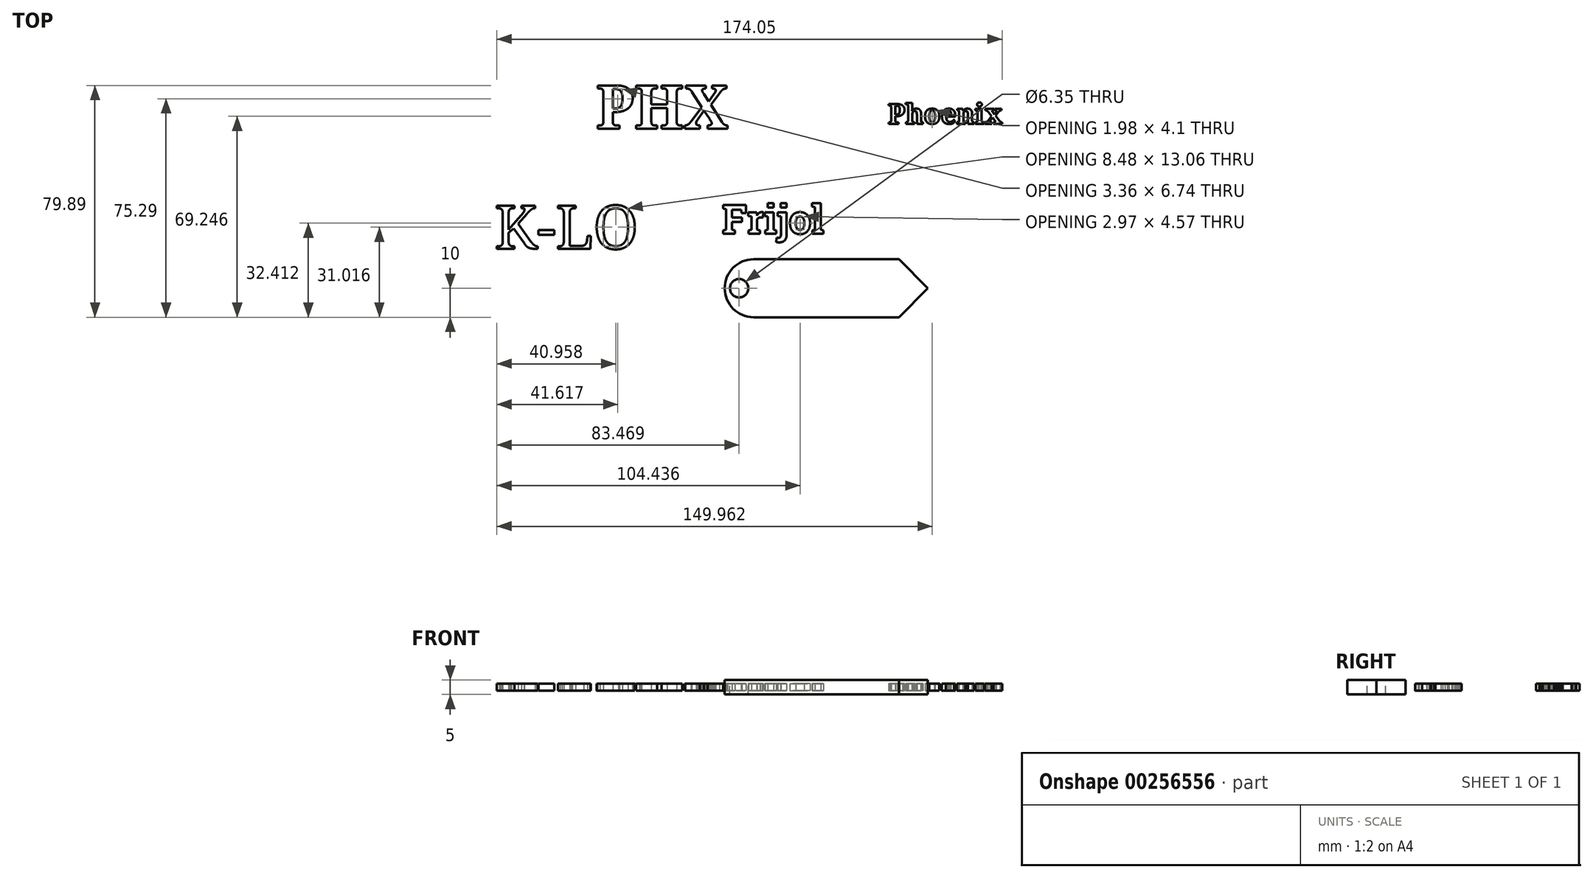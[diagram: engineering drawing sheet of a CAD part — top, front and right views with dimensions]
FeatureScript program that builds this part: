
annotation { "Feature Type Name" : "Feature", "Feature Type Description" : "" }
export const myFeature = defineFeature(function(context is Context, id is Id, definition is map)
    precondition{}
    {
        {
            var Q0;
            Q0=qCreatedBy(makeId("Top.planeOp"),FACE);
            var sketch = newSketch(context, id + "F0", { "sketchPlane" : qUnion([Q0])});
            skLineSegment(sketch, "E0.bottom", {"start": v(-24.92, 11.15) * mm, "end": v(25.08, 11.15) * mm});
            skLineSegment(sketch, "E0.top", {"start": v(-24.92, -8.85) * mm, "end": v(25.08, -8.85) * mm});
            skLineSegment(sketch, "E0.left", {"start": v(-24.92, 11.15) * mm, "end": v(-24.92, -8.85) * mm});
            skLineSegment(sketch, "E0.right", {"start": v(25.08, 11.15) * mm, "end": v(25.08, -8.85) * mm});
            skPoint(sketch, "E1", {"position": v(0.08, 1.15) * mm});
            skPoint(sketch, "E2", {"position": v(0.08, 11.15) * mm});
            skPoint(sketch, "E3", {"position": v(0.08, -8.85) * mm});
            skPoint(sketch, "E4", {"position": v(25.08, 1.15) * mm});
            skLineSegment(sketch, "E5", {"start": v(0.08, -8.85) * mm, "end": v(0.08, 11.15) * mm, "construction": true});
            skArc(sketch, "E6", {"start": v(-24.92, 11.15) * mm, "mid": v(-34.92, 1.15) * mm, "end": v(-24.92, -8.85) * mm});
            skPoint(sketch, "E7", {"position": v(35.08, 1.15) * mm});
            skLineSegment(sketch, "E8", {"start": v(25.08, -8.85) * mm, "end": v(35.08, 1.15) * mm});
            skLineSegment(sketch, "E9", {"start": v(25.08, 11.15) * mm, "end": v(35.08, 1.15) * mm});
            skPoint(sketch, "E10", {"position": v(-34.92, 1.15) * mm});
            skLineSegment(sketch, "E11", {"start": v(-24.92, 1.15) * mm, "end": v(-34.92, 1.15) * mm, "construction": true});
            skPoint(sketch, "E12", {"position": v(-29.92, 1.15) * mm});
            skSolve(sketch);
        }
        {
            var Q0;
            Q0=makeQuery(id+"F0.imprint","IMPRINT",FACE,{"disambiguationData":[TD([[makeQuery(id+"F0.imprint","IMPRINT",EDGE,{"derivedFrom":sQuery(id+"F0.wireOp",EDGE,"E0.bottom")}),-1.0]])]});
            var Q1;
            Q1=makeQuery(id+"F0.imprint","IMPRINT",FACE,{"disambiguationData":[TD([[makeQuery(id+"F0.imprint","IMPRINT",EDGE,{"derivedFrom":sQuery(id+"F0.wireOp",EDGE,"E0.left")}),-1.0]])]});
            var Q2;
            Q2=makeQuery(id+"F0.imprint","IMPRINT",FACE,{"disambiguationData":[TD([[makeQuery(id+"F0.imprint","IMPRINT",EDGE,{"derivedFrom":sQuery(id+"F0.wireOp",EDGE,"E0.right")}),1.0]])]});
            extrude(context, id + "F1", {"entities" : qUnion([Q0, Q1, Q2]), "endBound" : BoundingType.SYMMETRIC, "depth" : 5 * mm});
        }
        {
            var Q0;
            Q0=makeQuery(id+"F1.opExtrude","CAP_FACE",FACE,{"disambiguationData":[OSD([sQuery(id+"F0.wireOp",EDGE,"E0.bottom"),sQuery(id+"F0.wireOp",EDGE,"E0.top"),sQuery(id+"F0.wireOp",EDGE,"E6"),sQuery(id+"F0.wireOp",EDGE,"E8"),sQuery(id+"F0.wireOp",EDGE,"E9")])],"isStart":false});
            var sketch = newSketch(context, id + "F2", { "sketchPlane" : qUnion([Q0])});
            skLineSegment(sketch, "E13.bottom", {"start": v(-24.92, 11.15) * mm, "end": v(25.08, 11.15) * mm});
            skLineSegment(sketch, "E13.top", {"start": v(-24.92, -8.85) * mm, "end": v(25.08, -8.85) * mm});
            skLineSegment(sketch, "E13.left", {"start": v(-24.92, 11.15) * mm, "end": v(-24.92, -8.85) * mm});
            skLineSegment(sketch, "E13.right", {"start": v(25.08, 11.15) * mm, "end": v(25.08, -8.85) * mm});
            skPoint(sketch, "E14", {"position": v(0.08, 1.15) * mm});
            skPoint(sketch, "E15", {"position": v(0.08, 11.15) * mm});
            skPoint(sketch, "E16", {"position": v(0.08, -8.85) * mm});
            skPoint(sketch, "E17", {"position": v(25.08, 1.15) * mm});
            skLineSegment(sketch, "E18", {"start": v(0.08, -8.85) * mm, "end": v(0.08, 11.15) * mm, "construction": true});
            skArc(sketch, "E19", {"start": v(-24.92, 11.15) * mm, "mid": v(-34.92, 1.15) * mm, "end": v(-24.92, -8.85) * mm});
            skPoint(sketch, "E20", {"position": v(35.08, 1.15) * mm});
            skLineSegment(sketch, "E21", {"start": v(25.08, -8.85) * mm, "end": v(35.08, 1.15) * mm});
            skLineSegment(sketch, "E22", {"start": v(25.08, 11.15) * mm, "end": v(35.08, 1.15) * mm});
            skPoint(sketch, "E23", {"position": v(-34.92, 1.15) * mm});
            skLineSegment(sketch, "E24", {"start": v(-24.92, 1.15) * mm, "end": v(-34.92, 1.15) * mm, "construction": true});
            skPoint(sketch, "E25", {"position": v(-29.92, 1.15) * mm});
            skSolve(sketch);
        }
        {
            var Q0;
            Q0=sQuery(id+"F2.wireOp",VERTEX,"E25");
            var Q1;
            Q1=makeQuery(id+"F1.opExtrude","SWEPT_BODY",BODY,{"disambiguationData":[OSD([sQuery(id+"F0.wireOp",EDGE,"E0.bottom"),sQuery(id+"F0.wireOp",EDGE,"E0.top"),sQuery(id+"F0.wireOp",EDGE,"E6"),sQuery(id+"F0.wireOp",EDGE,"E8"),sQuery(id+"F0.wireOp",EDGE,"E9")])]});
            hole(context, id + "F3", {"style" : HoleStyle.SIMPLE, "endStyle" : HoleEndStyle.THROUGH, "holeDiameter" : 6.35 * mm, "isTappedThrough" : true, "tappedDepth" : 12.7 * mm, "tapClearance" : 3, "locations" : qUnion([Q0]), "scope" : qUnion([Q1]), "majorDiameter" : 6.35 * mm});
        }
        {
            var Q0;
            Q0=qCreatedBy(makeId("Top.planeOp"),FACE);
            var sketch = newSketch(context, id + "F4", { "sketchPlane" : qUnion([Q0])});
            skText(sketch, "E26", { "text": "Frijol", "fontName": "RobotoSlab-Bold.ttf"});
            const initialGuessF4  = {"E26": [-0.03581, 0.0199, 1, 0, 0.01]};
            skSetInitialGuess(sketch, initialGuessF4);
            skSolve(sketch);
        }
        {
            var Q0;
            Q0 = qSketchRegion(id + "F4", true);
            extrude(context, id + "F5", {"entities" : qUnion([Q0]), "endBound" : BoundingType.SYMMETRIC, "depth" : 2.5 * mm, "offsetDistance" : 25.4 * mm});
        }
        {
            var Q0;
            Q0=qCreatedBy(makeId("Top.planeOp"),FACE);
            var sketch = newSketch(context, id + "F6", { "sketchPlane" : qUnion([Q0])});
            skText(sketch, "E27", { "text": "PHX", "fontName": "NotoSerif-Bold.ttf"});
            skText(sketch, "E28", { "text": "Phoenix", "fontName": "NotoSerif-Bold.ttf"});
            skText(sketch, "E29", { "text": "K-LO", "fontName": "NotoSerif-Regular.ttf"});
            const initialGuessF6  = {"E27": [-0.07926, 0.05617, 1, 0, 0.015], "E28": [0.02126, 0.05784, 1, 0, 0.00684], "E29": [-0.11418, 0.01472, 1, 0, 0.015]};
            skSetInitialGuess(sketch, initialGuessF6);
            skSolve(sketch);
        }
        {
            var Q0;
            Q0 = qSketchRegion(id + "F6", true);
            extrude(context, id + "F7", {"entities" : qUnion([Q0]), "endBound" : BoundingType.SYMMETRIC, "depth" : 2.5 * mm, "offsetDistance" : 25.4 * mm});
        }
    });
